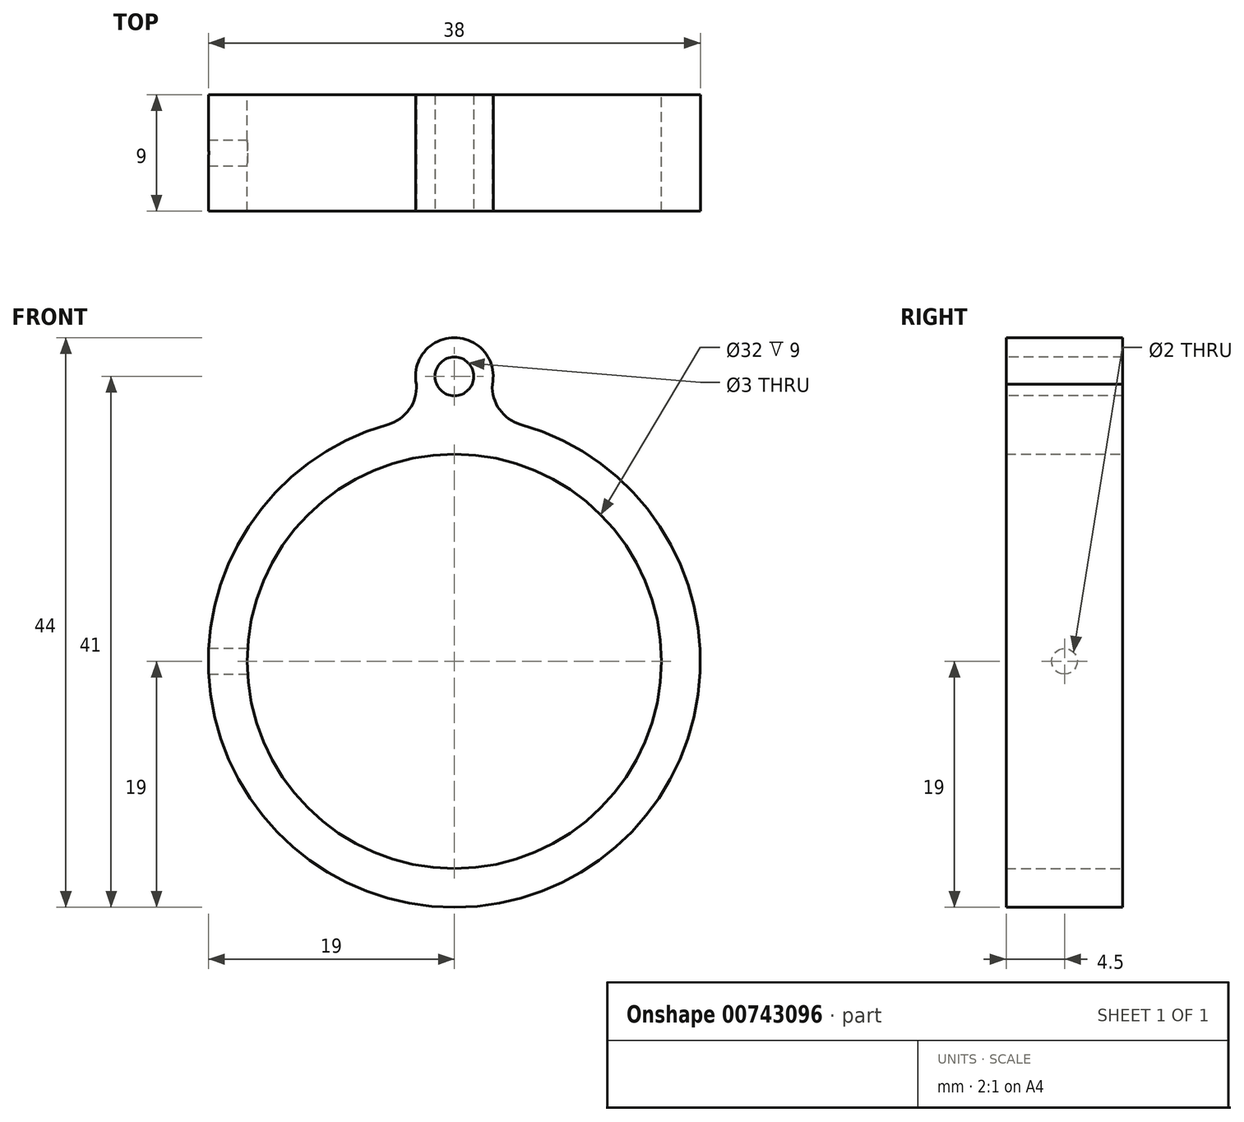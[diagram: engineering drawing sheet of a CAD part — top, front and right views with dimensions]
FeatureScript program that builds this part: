
annotation { "Feature Type Name" : "Feature", "Feature Type Description" : "" }
export const myFeature = defineFeature(function(context is Context, id is Id, definition is map)
    precondition{}
    {
        {
            var Q0;
            Q0=qCreatedBy(makeId("Front.planeOp"),FACE);
            var sketch = newSketch(context, id + "F0", { "sketchPlane" : qUnion([Q0])});
            skCircle(sketch, "E0", {"center": v(0, 0) * mm, "radius": 16 * mm});
            skCircle(sketch, "E1", {"center": v(0, 0) * mm, "radius": 19 * mm});
            skSolve(sketch);
        }
        {
            var Q0;
            Q0=qSketchRegion(id+"F0",true);
            extrude(context, id + "F1", {"entities" : qUnion([Q0]), "depth" : 9 * mm, "offsetDistance" : 25 * mm});
        }
        {
            var Q0;
            Q0=makeQuery(id+"F1.opExtrude","CAP_FACE",FACE,{"disambiguationData":[OSD([sQuery(id+"F0.wireOp",EDGE,"E0"),sQuery(id+"F0.wireOp",EDGE,"E1")])],"isStart":true});
            var sketch = newSketch(context, id + "F2", { "sketchPlane" : qUnion([Q0])});
            skCircle(sketch, "E2", {"center": v(0, 0) * mm, "radius": 19 * mm});
            skCircle(sketch, "E3", {"center": v(0, 0) * mm, "radius": 7.5 * mm});
            skSolve(sketch);
        }
        {
            var Q0;
            Q0=makeQuery(id+"F1.opExtrude","CAP_FACE",FACE,{"disambiguationData":[OSD([sQuery(id+"F0.wireOp",EDGE,"E0"),sQuery(id+"F0.wireOp",EDGE,"E1")])],"isStart":false});
            var sketch = newSketch(context, id + "F3", { "sketchPlane" : qUnion([Q0])});
            skArc(sketch, "E4.0", {"start": v(-17.22, 8.03) * mm, "mid": v(-19, 0) * mm, "end": v(-17.22, -8.03) * mm});
            skLineSegment(sketch, "E5", {"start": v(-7.7, -3.6) * mm, "end": v(-17.22, -8.03) * mm});
            skLineSegment(sketch, "E6.MirrorCS", {"start": v(-7.7, 3.6) * mm, "end": v(-17.22, 8.03) * mm});
            skArc(sketch, "E7.0", {"start": v(-7.7, -3.6) * mm, "mid": v(-8.5, 0) * mm, "end": v(-7.7, 3.6) * mm});
            skSolve(sketch);
        }
        {
            var Q0;
            Q0=qCreatedBy(makeId("Right.planeOp"),FACE);
            var sketch = newSketch(context, id + "F4", { "sketchPlane" : qUnion([Q0])});
            skLineSegment(sketch, "E8.0", {"start": v(3, -19) * mm, "end": v(3, 19) * mm});
            skLineSegment(sketch, "E9.0", {"start": v(-9, -19) * mm, "end": v(-9, 19) * mm});
            skCircle(sketch, "E10", {"center": v(-18, 0) * mm, "radius": 3 * mm});
            skSolve(sketch);
        }
        {
            var Q0;
            Q0=makeQuery(id+"F4.imprint","IMPRINT",FACE,{"disambiguationData":[TD([[makeQuery(id+"F4.imprint","IMPRINT",EDGE,{"derivedFrom":sQuery(id+"F4.wireOp",EDGE,"E10")}),1.0]])]});
            extrude(context, id + "F5", {"entities" : qUnion([Q0]), "operationType" : NewBodyOperationType.REMOVE, "endBound" : BoundingType.THROUGH_ALL, "oppositeDirection" : true, "depth" : 25 * mm, "offsetDistance" : 25 * mm});
        }
        {
            var Q0;
            {var subQ0=sQuery(id+"F3.wireOp",EDGE,"E5");var subQ4=makeQuery(id+"F1.opExtrude","CAP_EDGE",EDGE,{"disambiguationData":[OSD([sQuery(id+"F0.wireOp",EDGE,"E0")])],"isStart":false});var subQ5=makeQuery(id+"F3.imprint","INTERSECT",VERTEX,{"derivedFrom":[subQ4,subQ0]});Q0=makeQuery(id+"F3.imprint","IMPRINT",FACE,{"disambiguationData":[TD([[makeQuery(id+"F3.imprint","IMPRINT",EDGE,{"disambiguationData":[TD([[subQ5,-1.0]])],"derivedFrom":subQ4}),-1.0]])]});}
            var sketch = newSketch(context, id + "F6", { "sketchPlane" : qUnion([Q0])});
            skArc(sketch, "E11.0", {"start": v(-5.12, 18.3) * mm, "mid": v(0, 19) * mm, "end": v(5.12, 18.3) * mm});
            skArc(sketch, "E12", {"start": v(2.94, 21.4) * mm, "mid": v(0, 25) * mm, "end": v(-2.94, 21.4) * mm});
            skArc(sketch, "E13", {"start": v(-5.12, 18.3) * mm, "mid": v(-3.37, 19.63) * mm, "end": v(-3, 21.8) * mm});
            skArc(sketch, "E14", {"start": v(3, 21.8) * mm, "mid": v(3.37, 19.63) * mm, "end": v(5.12, 18.3) * mm});
            skCircle(sketch, "E15", {"center": v(0, 22) * mm, "radius": 1.5 * mm});
            skSolve(sketch);
        }
        {
            var Q0;
            Q0=qSketchRegion(id+"F6",true);
            extrude(context, id + "F7", {"entities" : qUnion([Q0]), "operationType" : NewBodyOperationType.ADD, "oppositeDirection" : true, "depth" : 9 * mm, "offsetDistance" : 25 * mm});
        }
        {
            var Q0;
            Q0=qCreatedBy(makeId("Right.planeOp"),FACE);
            var sketch = newSketch(context, id + "F8", { "sketchPlane" : qUnion([Q0])});
            skPoint(sketch, "E16", {"position": v(-4.5, 0) * mm});
            skSolve(sketch);
        }
        {
            var Q0;
            Q0=sQuery(id+"F8.wireOp",VERTEX,"E16");
            var Q1;
            Q1=makeQuery(id+"F1.opExtrude","SWEPT_BODY",BODY,{"disambiguationData":[OSD([sQuery(id+"F0.wireOp",EDGE,"E0"),sQuery(id+"F0.wireOp",EDGE,"E1")])]});
            hole(context, id + "F9", {"style" : HoleStyle.SIMPLE, "endStyle" : HoleEndStyle.BLIND, "holeDiameter" : 2 * mm, "majorDiameter" : 5 * mm, "holeDepth" : 50 * mm, "isTappedThrough" : true, "tappedDepth" : 12 * mm, "tapClearance" : 3, "startFromSketch" : true, "locations" : qUnion([Q0]), "scope" : qUnion([Q1])});
        }
    });
